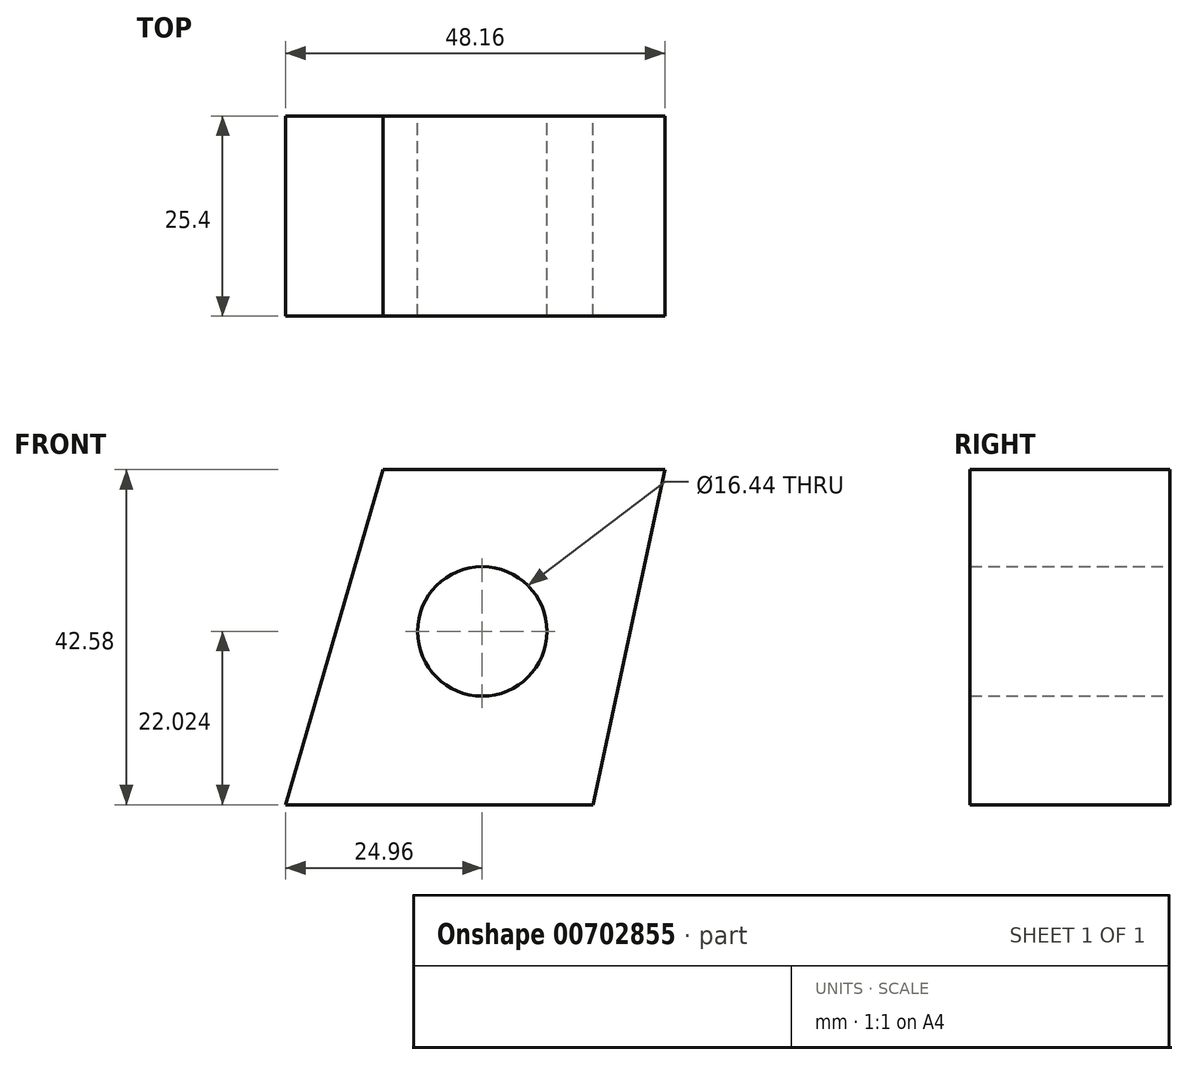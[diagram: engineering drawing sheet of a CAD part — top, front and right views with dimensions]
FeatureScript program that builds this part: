
annotation { "Feature Type Name" : "Feature", "Feature Type Description" : "" }
export const myFeature = defineFeature(function(context is Context, id is Id, definition is map)
    precondition{}
    {
        {
            var Q0;
            Q0=qCreatedBy(makeId("Front.planeOp"),FACE);
            var sketch = newSketch(context, id + "F0", { "sketchPlane" : qUnion([Q0])});
            skLineSegment(sketch, "E0", {"start": v(-28.63, -35.53) * mm, "end": v(10.42, -35.53) * mm});
            skLineSegment(sketch, "E1", {"start": v(10.42, -35.53) * mm, "end": v(19.53, 7.05) * mm});
            skLineSegment(sketch, "E2", {"start": v(19.53, 7.05) * mm, "end": v(-16.3, 7.05) * mm});
            skLineSegment(sketch, "E3", {"start": v(-16.3, 7.05) * mm, "end": v(-28.63, -35.53) * mm});
            skCircle(sketch, "E4", {"center": v(-3.67, -13.5) * mm, "radius": 8.22 * mm});
            skSolve(sketch);
        }
        {
            var Q0;
            Q0 = qSketchRegion(id + "F0", true);
            extrude(context, id + "F1", {"entities" : qUnion([Q0]), "depth" : 25.4 * mm, "offsetDistance" : 25.4 * mm});
        }
    });
